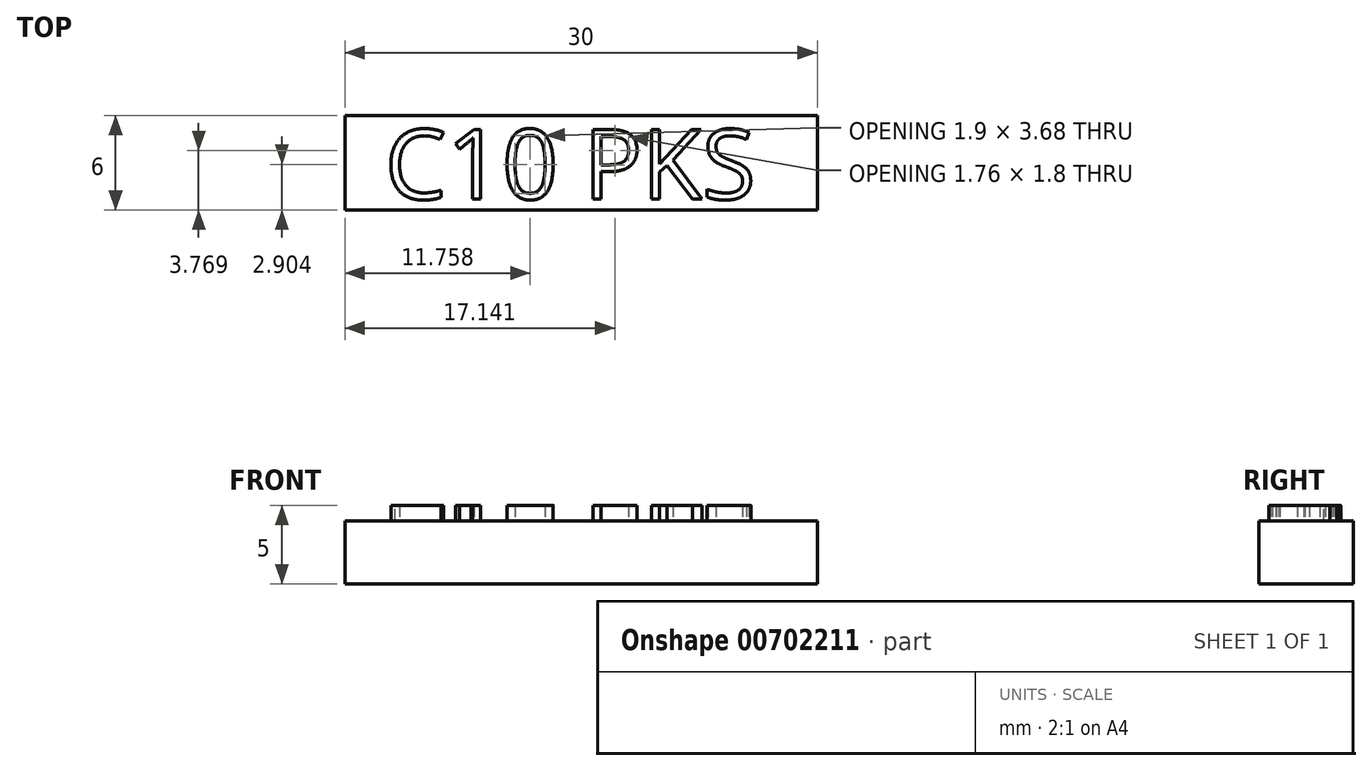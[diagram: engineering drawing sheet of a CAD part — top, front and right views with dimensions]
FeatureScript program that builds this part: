
annotation { "Feature Type Name" : "Feature", "Feature Type Description" : "" }
export const myFeature = defineFeature(function(context is Context, id is Id, definition is map)
    precondition{}
    {
        {
            var Q0;
            Q0=qCreatedBy(makeId("Top.planeOp"),FACE);
            var sketch = newSketch(context, id + "F0", { "sketchPlane" : qUnion([Q0])});
            skLineSegment(sketch, "E0.bottom", {"start": v(-44.15, 50.56) * mm, "end": v(-14.15, 50.56) * mm});
            skLineSegment(sketch, "E0.top", {"start": v(-44.15, 44.56) * mm, "end": v(-14.15, 44.56) * mm});
            skLineSegment(sketch, "E0.left", {"start": v(-44.15, 50.56) * mm, "end": v(-44.15, 44.56) * mm});
            skLineSegment(sketch, "E0.right", {"start": v(-14.15, 50.56) * mm, "end": v(-14.15, 44.56) * mm});
            skSolve(sketch);
        }
        {
            var Q0;
            Q0=makeQuery(id+"F0.imprint","IMPRINT",FACE,{"disambiguationData":[TD([[makeQuery(id+"F0.imprint","IMPRINT",EDGE,{"derivedFrom":sQuery(id+"F0.wireOp",EDGE,"E0.bottom")}),-1.0]])]});
            extrude(context, id + "F1", {"entities" : qUnion([Q0]), "depth" : 4 * mm, "offsetDistance" : 25.4 * mm});
        }
        {
            var Q0;
            Q0=makeQuery(id+"F1.opExtrude","CAP_FACE",FACE,{"disambiguationData":[OSD([sQuery(id+"F0.wireOp",EDGE,"E0.bottom"),sQuery(id+"F0.wireOp",EDGE,"E0.top"),sQuery(id+"F0.wireOp",EDGE,"E0.left"),sQuery(id+"F0.wireOp",EDGE,"E0.right")])],"isStart":false});
            var sketch = newSketch(context, id + "F2", { "sketchPlane" : qUnion([Q0])});
            skText(sketch, "E1", { "text": "C10 PKS", "fontName": "OpenSans-Regular.ttf"});
            const initialGuessF2  = {"E1": [-0.04161, 0.04525, 1, 0, 0.00446]};
            skSetInitialGuess(sketch, initialGuessF2);
            skSolve(sketch);
        }
        {
            var Q0;
            Q0 = qSketchRegion(id + "F2", true);
            extrude(context, id + "F3", {"entities" : qUnion([Q0]), "depth" : 1 * mm, "offsetDistance" : 25.4 * mm});
        }
        {
            var Q0;
            Q0 = qSketchRegion(id + "F0", true);
            extrude(context, id + "F4", {"entities" : qUnion([Q0]), "depth" : 4 * mm, "offsetDistance" : 25.4 * mm});
        }
        {
            var Q0;
            Q0 = qSketchRegion(id + "F0", true);
            extrude(context, id + "F5", {"entities" : qUnion([Q0]), "operationType" : NewBodyOperationType.ADD, "depth" : 2 * mm, "offsetDistance" : 25.4 * mm});
        }
    });
